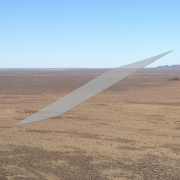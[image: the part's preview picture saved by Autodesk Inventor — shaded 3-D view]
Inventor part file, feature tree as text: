
AUTODESK INVENTOR PART (.ipt)
format: ipt  version: 2014 SP1 (Build 180222100, 222)  size: 153,088 bytes
history: native  units: in
note: dims shown in document units (in); Inventor stores cm internally (conversion verified against a paired STEP export)
features: sketch x3, sweep x1, extrude x1, other x1
ambient origin geometry x8: Origin, YZ Plane, XZ Plane, XY Plane, X Axis, Y Axis, Z Axis, Center Point
bodies: Body1 (feature_tree)
feature tree (6):
  sweep  "Sweep2"
  extrude  "Extrusion3"  TaperAngle=0.0deg  [1 undecoded]
  sketch  "Sketch3"  dims[d6=0.0in d7=275.0in d8=90.0in]
  other  "2D Equation Curve2"
  sketch  "Sketch4"  dims[d10=0.25in d11=0.0in]
  sketch  "Sketch8"  dims[d28=2.0in d29=2.0in d32=2.0in d33=300.0in d34=1.1853in d35=238.0in d36=277.0in d37=300.0in d38=0.0in]
note: 1 required parameter value undecoded (feature->parameter linkage not recoverable at this tier; creation-order binding heuristic only, values carry confidence <= 0.55)
